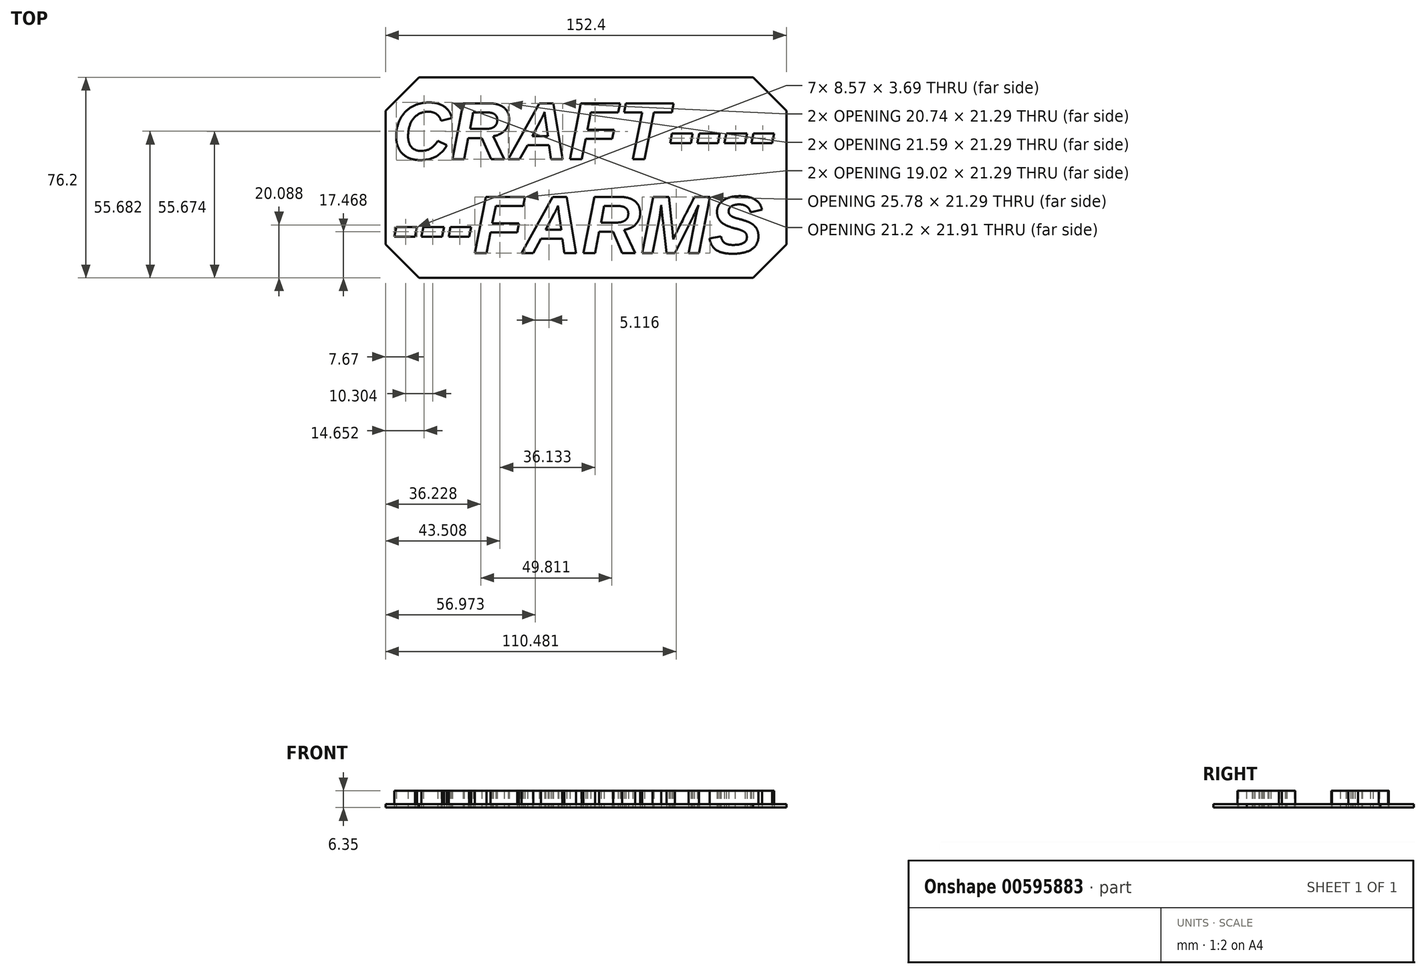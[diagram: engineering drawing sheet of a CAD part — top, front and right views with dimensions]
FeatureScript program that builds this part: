
annotation { "Feature Type Name" : "Feature", "Feature Type Description" : "" }
export const myFeature = defineFeature(function(context is Context, id is Id, definition is map)
    precondition{}
    {
        {
            var Q0;
            Q0=qCreatedBy(makeId("Top.planeOp"),FACE);
            var sketch = newSketch(context, id + "F0", { "sketchPlane" : qUnion([Q0])});
            skLineSegment(sketch, "E0.bottom", {"start": v(-76.2, 38.1) * mm, "end": v(76.2, 38.1) * mm});
            skLineSegment(sketch, "E0.top", {"start": v(-76.2, -38.1) * mm, "end": v(76.2, -38.1) * mm});
            skLineSegment(sketch, "E0.left", {"start": v(-76.2, 38.1) * mm, "end": v(-76.2, -38.1) * mm});
            skLineSegment(sketch, "E0.right", {"start": v(76.2, 38.1) * mm, "end": v(76.2, -38.1) * mm});
            skPoint(sketch, "E0.middle", {"position": v(0, 0) * mm});
            skPoint(sketch, "E1", {"position": v(-73.66, 29.21) * mm});
            skText(sketch, "E2", { "text": "CRAFT----\n---FARMS", "fontName": "Arimo-BoldItalic.ttf"});
            skLineSegment(sketch, "E3", {"start": v(-76.2, 25.4) * mm, "end": v(-63.5, 38.1) * mm});
            skLineSegment(sketch, "E4.MirrorCS", {"start": v(76.2, 25.4) * mm, "end": v(63.5, 38.1) * mm});
            skLineSegment(sketch, "E5.MirrorCS", {"start": v(-76.2, -25.4) * mm, "end": v(-63.5, -38.1) * mm});
            skLineSegment(sketch, "E6.MirrorCS", {"start": v(76.2, -25.4) * mm, "end": v(63.5, -38.1) * mm});
            const initialGuessF0  = {"E2": [-0.07366, 0.00693, 1, 0, 0.02228]};
            skSetInitialGuess(sketch, initialGuessF0);
            skSolve(sketch);
        }
        {
            var Q0;
            Q0=makeQuery(id+"F0.imprint","IMPRINT",FACE,{"disambiguationData":[TD([[makeQuery(id+"F0.imprint","IMPRINT",EDGE,{"derivedFrom":sQuery(id+"F0.wireOp",EDGE,"E2.sketch_text.stroke-97")}),-1.0]])]});
            var Q1;
            Q1=makeQuery(id+"F0.imprint","IMPRINT",FACE,{"disambiguationData":[TD([[makeQuery(id+"F0.imprint","IMPRINT",EDGE,{"derivedFrom":sQuery(id+"F0.wireOp",EDGE,"E2.sketch_text.stroke-93")}),-1.0]])]});
            var Q2;
            Q2=makeQuery(id+"F0.imprint","IMPRINT",FACE,{"disambiguationData":[TD([[makeQuery(id+"F0.imprint","IMPRINT",EDGE,{"derivedFrom":sQuery(id+"F0.wireOp",EDGE,"E2.sketch_text.stroke-89")}),-1.0]])]});
            var Q3;
            Q3=makeQuery(id+"F0.imprint","IMPRINT",FACE,{"disambiguationData":[TD([[makeQuery(id+"F0.imprint","IMPRINT",EDGE,{"derivedFrom":sQuery(id+"F0.wireOp",EDGE,"E2.sketch_text.stroke-85")}),-1.0]])]});
            var Q4;
            Q4=makeQuery(id+"F0.imprint","IMPRINT",FACE,{"disambiguationData":[TD([[makeQuery(id+"F0.imprint","IMPRINT",EDGE,{"derivedFrom":sQuery(id+"F0.wireOp",EDGE,"E2.sketch_text.stroke-0")}),-1.0]])]});
            var Q5;
            Q5=makeQuery(id+"F0.imprint","IMPRINT",FACE,{"disambiguationData":[TD([[makeQuery(id+"F0.imprint","IMPRINT",EDGE,{"derivedFrom":sQuery(id+"F0.wireOp",EDGE,"E2.sketch_text.stroke-18")}),-1.0]])]});
            var Q6;
            Q6=makeQuery(id+"F0.imprint","IMPRINT",FACE,{"disambiguationData":[TD([[makeQuery(id+"F0.imprint","IMPRINT",EDGE,{"derivedFrom":sQuery(id+"F0.wireOp",EDGE,"E2.sketch_text.stroke-38")}),-1.0]])]});
            var Q7;
            Q7=makeQuery(id+"F0.imprint","IMPRINT",FACE,{"disambiguationData":[TD([[makeQuery(id+"F0.imprint","IMPRINT",EDGE,{"derivedFrom":sQuery(id+"F0.wireOp",EDGE,"E2.sketch_text.stroke-51")}),-1.0]])]});
            var Q8;
            Q8=makeQuery(id+"F0.imprint","IMPRINT",FACE,{"disambiguationData":[TD([[makeQuery(id+"F0.imprint","IMPRINT",EDGE,{"derivedFrom":sQuery(id+"F0.wireOp",EDGE,"E2.sketch_text.stroke-61")}),-1.0]])]});
            var Q9;
            Q9=makeQuery(id+"F0.imprint","IMPRINT",FACE,{"disambiguationData":[TD([[makeQuery(id+"F0.imprint","IMPRINT",EDGE,{"derivedFrom":sQuery(id+"F0.wireOp",EDGE,"E2.sketch_text.stroke-69")}),-1.0]])]});
            var Q10;
            Q10=makeQuery(id+"F0.imprint","IMPRINT",FACE,{"disambiguationData":[TD([[makeQuery(id+"F0.imprint","IMPRINT",EDGE,{"derivedFrom":sQuery(id+"F0.wireOp",EDGE,"E2.sketch_text.stroke-73")}),-1.0]])]});
            var Q11;
            Q11=makeQuery(id+"F0.imprint","IMPRINT",FACE,{"disambiguationData":[TD([[makeQuery(id+"F0.imprint","IMPRINT",EDGE,{"derivedFrom":sQuery(id+"F0.wireOp",EDGE,"E2.sketch_text.stroke-77")}),-1.0]])]});
            var Q12;
            Q12=makeQuery(id+"F0.imprint","IMPRINT",FACE,{"disambiguationData":[TD([[makeQuery(id+"F0.imprint","IMPRINT",EDGE,{"derivedFrom":sQuery(id+"F0.wireOp",EDGE,"E2.sketch_text.stroke-81")}),-1.0]])]});
            var Q13;
            Q13=makeQuery(id+"F0.imprint","IMPRINT",FACE,{"disambiguationData":[TD([[makeQuery(id+"F0.imprint","IMPRINT",EDGE,{"derivedFrom":sQuery(id+"F0.wireOp",EDGE,"E2.sketch_text.stroke-160")}),-1.0]])]});
            var Q14;
            Q14=makeQuery(id+"F0.imprint","IMPRINT",FACE,{"disambiguationData":[TD([[makeQuery(id+"F0.imprint","IMPRINT",EDGE,{"derivedFrom":sQuery(id+"F0.wireOp",EDGE,"E2.sketch_text.stroke-140")}),-1.0]])]});
            var Q15;
            Q15=makeQuery(id+"F0.imprint","IMPRINT",FACE,{"disambiguationData":[TD([[makeQuery(id+"F0.imprint","IMPRINT",EDGE,{"derivedFrom":sQuery(id+"F0.wireOp",EDGE,"E2.sketch_text.stroke-120")}),-1.0]])]});
            var Q16;
            Q16=makeQuery(id+"F0.imprint","IMPRINT",FACE,{"disambiguationData":[TD([[makeQuery(id+"F0.imprint","IMPRINT",EDGE,{"derivedFrom":sQuery(id+"F0.wireOp",EDGE,"E2.sketch_text.stroke-107")}),-1.0]])]});
            extrude(context, id + "F1", {"entities" : qUnion([Q0, Q1, Q2, Q3, Q4, Q5, Q6, Q7, Q8, Q9, Q10, Q11, Q12, Q13, Q14, Q15, Q16]), "depth" : 6.35 * mm, "offsetDistance" : 25.4 * mm});
        }
        {
            var Q0;
            Q0=makeQuery(id+"F0.imprint","IMPRINT",FACE,{"disambiguationData":[TD([[makeQuery(id+"F0.imprint","IMPRINT",EDGE,{"derivedFrom":sQuery(id+"F0.wireOp",EDGE,"E2.sketch_text.stroke-0")}),1.0]])]});
            var Q1;
            Q1=makeQuery(id+"F0.imprint","IMPRINT",FACE,{"disambiguationData":[TD([[makeQuery(id+"F0.imprint","IMPRINT",EDGE,{"derivedFrom":sQuery(id+"F0.wireOp",EDGE,"E2.sketch_text.stroke-31")}),1.0]])]});
            var Q2;
            Q2=makeQuery(id+"F0.imprint","IMPRINT",FACE,{"disambiguationData":[TD([[makeQuery(id+"F0.imprint","IMPRINT",EDGE,{"derivedFrom":sQuery(id+"F0.wireOp",EDGE,"E2.sketch_text.stroke-46")}),1.0]])]});
            var Q3;
            Q3=makeQuery(id+"F0.imprint","IMPRINT",FACE,{"disambiguationData":[TD([[makeQuery(id+"F0.imprint","IMPRINT",EDGE,{"derivedFrom":sQuery(id+"F0.wireOp",EDGE,"E2.sketch_text.stroke-115")}),1.0]])]});
            var Q4;
            Q4=makeQuery(id+"F0.imprint","IMPRINT",FACE,{"disambiguationData":[TD([[makeQuery(id+"F0.imprint","IMPRINT",EDGE,{"derivedFrom":sQuery(id+"F0.wireOp",EDGE,"E2.sketch_text.stroke-133")}),1.0]])]});
            extrude(context, id + "F2", {"entities" : qUnion([Q0, Q1, Q2, Q3, Q4]), "depth" : 1.27 * mm, "offsetDistance" : 25.4 * mm});
        }
    });
